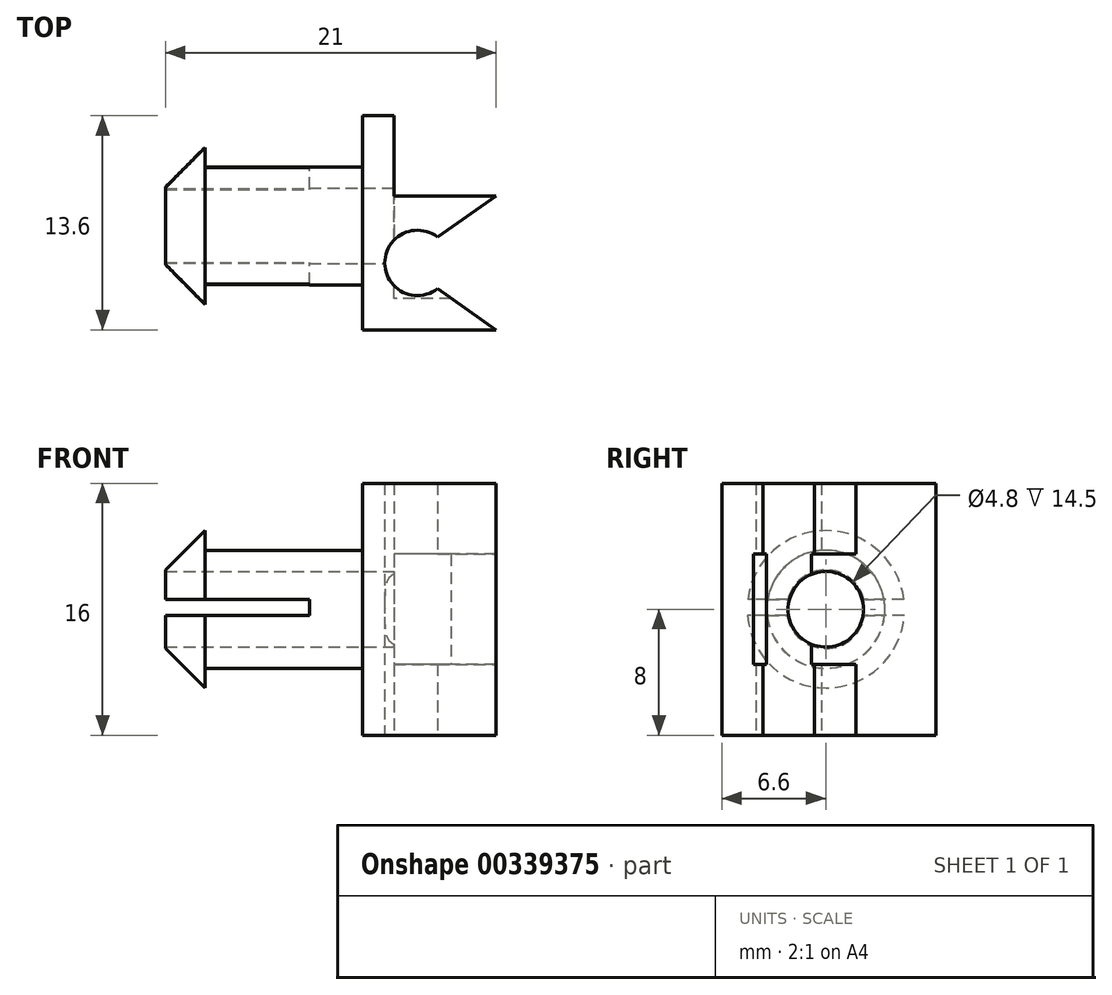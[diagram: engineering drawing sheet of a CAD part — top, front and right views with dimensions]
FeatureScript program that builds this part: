
annotation { "Feature Type Name" : "Feature", "Feature Type Description" : "" }
export const myFeature = defineFeature(function(context is Context, id is Id, definition is map)
    precondition{}
    {
        {
            var Q0;
            Q0=qCreatedBy(makeId("Top.planeOp"),FACE);
            var sketch = newSketch(context, id + "F0", { "sketchPlane" : qUnion([Q0])});
            skLineSegment(sketch, "E0", {"start": v(0, 13.6) * mm, "end": v(0, 0) * mm});
            skLineSegment(sketch, "E1", {"start": v(0, 0) * mm, "end": v(8.5, 0) * mm});
            skLineSegment(sketch, "E2", {"start": v(8.5, 8.5) * mm, "end": v(2, 8.5) * mm});
            skLineSegment(sketch, "E3", {"start": v(2, 8.5) * mm, "end": v(2, 13.6) * mm});
            skLineSegment(sketch, "E4", {"start": v(2, 13.6) * mm, "end": v(0, 13.6) * mm});
            skArc(sketch, "E5", {"start": v(4.77, 5.89) * mm, "mid": v(1.42, 4.25) * mm, "end": v(4.77, 2.61) * mm});
            skLineSegment(sketch, "E6", {"start": v(8.5, 8.5) * mm, "end": v(4.77, 5.89) * mm});
            skLineSegment(sketch, "E7", {"start": v(8.5, 0) * mm, "end": v(4.77, 2.61) * mm});
            skSolve(sketch);
        }
        {
            var Q0;
            Q0 = qSketchRegion(id + "F0", true);
            extrude(context, id + "F1", {"entities" : qUnion([Q0]), "depth" : 16 * mm});
        }
        {
            var Q0;
            Q0=makeQuery(id+"F1.opExtrude","SWEPT_FACE",FACE,{"disambiguationData":[OSD([sQuery(id+"F0.wireOp",EDGE,"E2")])]});
            var sketch = newSketch(context, id + "F2", { "sketchPlane" : qUnion([Q0])});
            skLineSegment(sketch, "E8.bottom", {"start": v(-8.5, 4.5) * mm, "end": v(-2, 4.5) * mm});
            skLineSegment(sketch, "E8.top", {"start": v(-8.5, 11.5) * mm, "end": v(-2, 11.5) * mm});
            skLineSegment(sketch, "E8.left", {"start": v(-8.5, 4.5) * mm, "end": v(-8.5, 11.5) * mm});
            skLineSegment(sketch, "E8.right", {"start": v(-2, 4.5) * mm, "end": v(-2, 11.5) * mm});
            skSolve(sketch);
        }
        {
            var Q0;
            Q0=makeQuery(id+"F2.imprint","IMPRINT",FACE,{"disambiguationData":[TD([[makeQuery(id+"F2.imprint","IMPRINT",EDGE,{"derivedFrom":sQuery(id+"F2.wireOp",EDGE,"E8.bottom")}),1.0]])]});
            extrude(context, id + "F3", {"entities" : qUnion([Q0]), "operationType" : NewBodyOperationType.REMOVE, "oppositeDirection" : true, "depth" : 6.5 * mm});
        }
        {
            var Q0;
            Q0=makeQuery(id+"F1.opExtrude","SWEPT_FACE",FACE,{"disambiguationData":[OSD([sQuery(id+"F0.wireOp",EDGE,"E0")])]});
            var sketch = newSketch(context, id + "F4", { "sketchPlane" : qUnion([Q0])});
            skCircle(sketch, "E9", {"center": v(-6.6, 8) * mm, "radius": 3.75 * mm});
            skCircle(sketch, "E10", {"center": v(-6.6, 8) * mm, "radius": 2.4 * mm});
            skSolve(sketch);
        }
        {
            var Q0;
            Q0=makeQuery(id+"F4.imprint","IMPRINT",FACE,{"disambiguationData":[TD([[makeQuery(id+"F4.imprint","IMPRINT",EDGE,{"derivedFrom":sQuery(id+"F4.wireOp",EDGE,"E9")}),1.0]])]});
            extrude(context, id + "F5", {"entities" : qUnion([Q0]), "operationType" : NewBodyOperationType.ADD, "depth" : 10 * mm});
        }
        {
            var Q0;
            Q0=makeQuery(id+"F5.boolean.opBoolean","SPLIT",FACE,{"disambiguationData":[TD([makeQuery(id+"F5.opExtrude","SWEPT_FACE",FACE,{"disambiguationData":[OSD([sQuery(id+"F4.wireOp",EDGE,"E10")])]})])],"derivedFrom":makeQuery(id+"F1.opExtrude","SWEPT_FACE",FACE,{"disambiguationData":[OSD([sQuery(id+"F0.wireOp",EDGE,"E0")])]})});
            extrude(context, id + "F6", {"entities" : qUnion([Q0]), "operationType" : NewBodyOperationType.REMOVE, "oppositeDirection" : true, "depth" : 8 * mm});
        }
        {
            var Q0;
            Q0=makeQuery(id+"F5.opExtrude","CAP_FACE",FACE,{"disambiguationData":[OSD([sQuery(id+"F4.wireOp",EDGE,"E9"),sQuery(id+"F4.wireOp",EDGE,"E10")])],"isStart":false});
            var sketch = newSketch(context, id + "F7", { "sketchPlane" : qUnion([Q0])});
            skCircle(sketch, "E11", {"center": v(-6.6, 8) * mm, "radius": 5 * mm});
            skSolve(sketch);
        }
        {
            var Q0;
            Q0 = qSketchRegion(id + "F7", true);
            extrude(context, id + "F8", {"entities" : qUnion([Q0]), "operationType" : NewBodyOperationType.ADD, "depth" : 2.5 * mm});
        }
        {
            var Q0;
            {var subQ0=sQuery(id+"F4.wireOp",EDGE,"E10");Q0=makeQuery(id+"F8.boolean.opBoolean","SPLIT",FACE,{"disambiguationData":[TD([makeQuery(id+"F5.opExtrude","SWEPT_FACE",FACE,{"disambiguationData":[OSD([subQ0])]})])],"derivedFrom":makeQuery(id+"F8.opExtrude","CAP_FACE",FACE,{"disambiguationData":[OSD([sQuery(id+"F7.wireOp",EDGE,"E11")])],"isStart":true})});}
            extrude(context, id + "F9", {"entities" : qUnion([Q0]), "operationType" : NewBodyOperationType.REMOVE, "oppositeDirection" : true, "depth" : 5 * mm});
        }
        {
            var Q0;
            Q0=makeQuery(id+"F8.opExtrude","CAP_EDGE",EDGE,{"disambiguationData":[OSD([sQuery(id+"F7.wireOp",EDGE,"E11")])],"isStart":false});
            chamfer(context, id + "F10", {"entities" : qUnion([Q0]), "chamferType" : ChamferType.OFFSET_ANGLE, "width" : 2.5 * mm, "oppositeDirection" : false, "angle" : 45 * degree, "tangentPropagation" : true});
        }
        {
            var Q0;
            Q0=makeQuery(id+"F1.opExtrude","SWEPT_FACE",FACE,{"disambiguationData":[OSD([sQuery(id+"F0.wireOp",EDGE,"E4")])]});
            var sketch = newSketch(context, id + "F11", { "sketchPlane" : qUnion([Q0])});
            skLineSegment(sketch, "E12.bottom", {"start": v(3.36, 8.6) * mm, "end": v(12.59, 8.6) * mm});
            skLineSegment(sketch, "E12.top", {"start": v(3.36, 7.6) * mm, "end": v(12.59, 7.6) * mm});
            skLineSegment(sketch, "E12.left", {"start": v(3.36, 8.6) * mm, "end": v(3.36, 7.6) * mm});
            skLineSegment(sketch, "E12.right", {"start": v(12.59, 8.6) * mm, "end": v(12.59, 7.6) * mm});
            skSolve(sketch);
        }
        {
            var Q0;
            Q0=makeQuery(id+"F11.imprint","IMPRINT",FACE,{"disambiguationData":[TD([[makeQuery(id+"F11.imprint","IMPRINT",EDGE,{"derivedFrom":sQuery(id+"F11.wireOp",EDGE,"E12.bottom")}),-1.0]])]});
            extrude(context, id + "F12", {"entities" : qUnion([Q0]), "operationType" : NewBodyOperationType.REMOVE, "oppositeDirection" : true, "depth" : 25 * mm});
        }
    });
